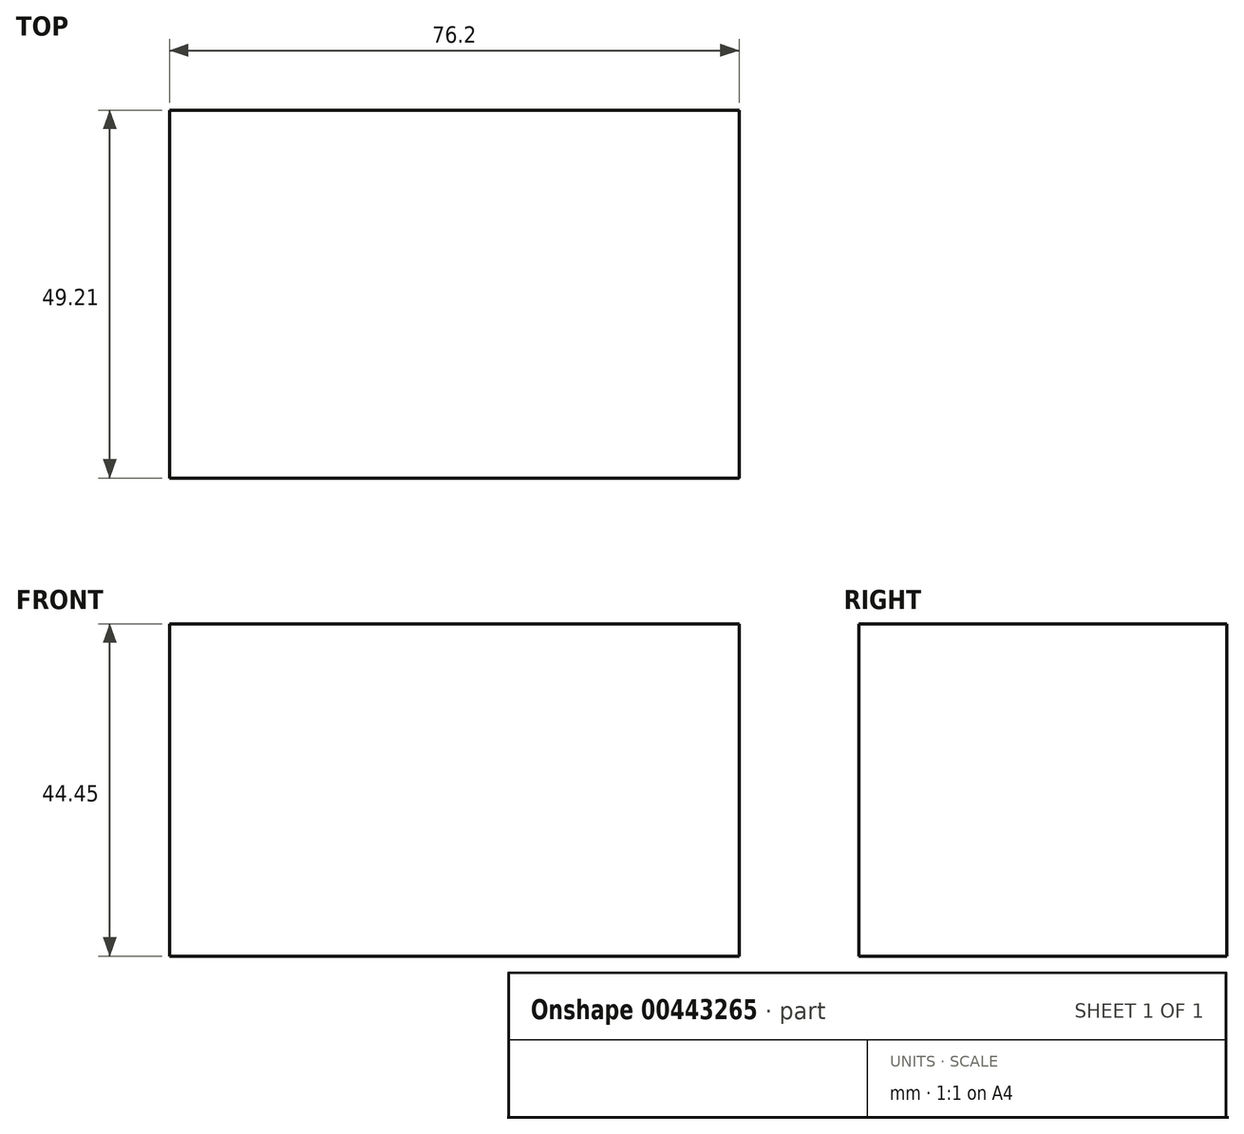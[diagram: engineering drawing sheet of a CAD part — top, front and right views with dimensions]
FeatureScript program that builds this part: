
annotation { "Feature Type Name" : "Feature", "Feature Type Description" : "" }
export const myFeature = defineFeature(function(context is Context, id is Id, definition is map)
    precondition{}
    {
        {
            var Q0;
            Q0=qCreatedBy(makeId("Top.planeOp"),FACE);
            var sketch = newSketch(context, id + "F0", { "sketchPlane" : qUnion([Q0])});
            skLineSegment(sketch, "E0.bottom", {"start": v(0, 0) * mm, "end": v(76.2, 0) * mm});
            skLineSegment(sketch, "E0.top", {"start": v(0, 49.21) * mm, "end": v(76.2, 49.21) * mm});
            skLineSegment(sketch, "E0.left", {"start": v(0, 0) * mm, "end": v(0, 49.21) * mm});
            skLineSegment(sketch, "E0.right", {"start": v(76.2, 0) * mm, "end": v(76.2, 49.21) * mm});
            skSolve(sketch);
        }
        {
            var Q0;
            Q0 = qSketchRegion(id + "F0", true);
            extrude(context, id + "F1", {"entities" : qUnion([Q0]), "depth" : 44.45 * mm});
        }
    });
